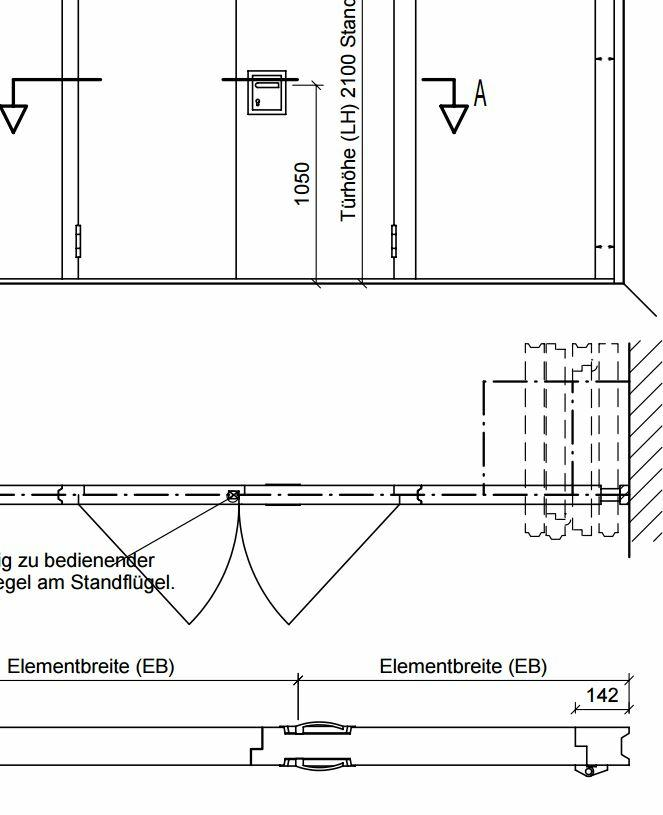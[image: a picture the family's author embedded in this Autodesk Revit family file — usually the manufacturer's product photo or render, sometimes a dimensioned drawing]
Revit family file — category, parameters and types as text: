
# Revit family: Walls_Moving_walls_Komandor_MAW_110_without_door_Z6
name_source: partatom
category: Generic Models
revit_build: Autodesk Revit 2014 (Build: 20130308_1515(x64)
units: mm (PartAtom-declared; Revit-internal decimal feet)

## types (1)
- Walls_Moving_walls_Komandor_MAW_110_without_door_Z6
    2nd Bar Distance = 5500 mm  [stored 18.0446 ft]
    BIMobject category = Folding & Moving Walls
    COBIe Type Category = Wall MOVABLE
    Design country = Poland
    Edition number = 1
    IFC Classification = Wall
    Installation instructions = http://www.komandorwalls.com
    Manufacturer country = Poland
    Manufacturer name = Komandor
    Masterformat 2014 Code = 07 42 00
    Masterformat 2014 Description = Wall Panels
    Material main = Aluminium
    Material secondary = MDF
    NBS Reference Code = 25-30-20-80
    NBS Reference Description = Sliding Stacking Panel Partition Systems
    Nominal height = 0
    Nominal width = 0
    OmniClass Code = 23-15 13 19
    OmniClass Description = Wall Panels
    Panel Material = Veneer, LF-2
    Product Guid = f88639dd-7851-4d73-ba37-f0ca554d38d5
    Product SKU = maw110
    Product data url = https://bimobject.com
    Product family = Walls
    Product group = MAW
    Profile Material = Komandor_Aluminum
    QR code = http://bimobject.com
    UNSPSC Code = 301615
    Uniclass 1.4 Code = L83122
    Uniclass 1.4 Description = Wall units
    Uniclass 2.0 Code = SS-25-30-20-80
    Uniclass 2.0 Description = Sliding Stacking Panel Partition Systems
    Uniclass 2015 Code = EF_25
    Uniclass 2015 Name = Wall and barrier elements
    Uniformat II Code = C3010
    Uniformat II Description = Wall Finishes
    Weight Net (Kg) = 0
    Youtube clip = https://www.youtube.com

note: [stored X ft] marks values corroborated as IEEE doubles in the binary element streams (Revit-internal decimal feet)

## geometry (parser evidence)
native form markers: Sweep x41
no freeform markers — native parametric forms only
